# Revit family: BTSMP-LMI
name_source: partatom
category: Communication Devices
units: mm (PartAtom-declared; Revit-internal decimal feet)

## family parameters
Cut with Voids When Loaded = No
Host = Face
Maintain Annotation Orientation = No
OmniClass Number = 23.85.80.11.27
OmniClass Title = Lighting Controls
Part Type = Normal
Room Calculation Point = No
Round Connector Dimension = Use Diameter
Shared = Yes

## types (1)
- BTSMP
    Assembly Code = D5090
    Black = Paint -  Carbon Black
    Certifications = • Conforms with UL STD 508, UL STD 244A
    Coverage = 1:1 (Mounting Height : Coverage Radius);
Up to 14ft
    Default Elevation = 48 "
    Description = The Passive-Infrared Bluetooth sensor module, or BTSMP, is the newest series of the  Control Solutions Bluetooth Sensor family. Perfect for architectural applications, it is smaller, more cost effective, seamlessly integrates with all luminaires and provides simple dimming control using the control app.
    Features = Passive Infrared (PIR) sensing technology provides excellent major
motion detection
• Wireless programming using HCS control mobile app
• 0-10V dimming control
• Single/Dual motion sensor timer modes
• Daylight sensor with multiple daylight harvesting modes
• Compact, discrete, low profile fixture sensor
    Manufacturer = NX Lighting Controls
    Model = Low Mount Indoor Sensor Module
    Mounting = Up to 14 ft
    Sensor Type = Passive Infrared
    Type Comments = Bluetooth® Low Mount Indoor Sensor Module
    URL = https://www.currentlighting.com
    Warranty = 5-Years Warranty
    White = Paint -  Matte White
    Width = 1.6 "

## geometry (parser evidence)
native form markers: Sweep x2
no freeform markers — native parametric forms only
